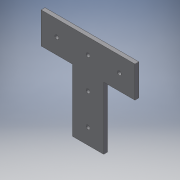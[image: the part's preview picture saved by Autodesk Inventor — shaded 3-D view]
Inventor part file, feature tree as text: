
AUTODESK INVENTOR PART (.ipt)
format: ipt  version: 2018 (Build 220112000, 112)  size: 117,248 bytes
history: native  units: in
note: dims shown in document units (in); Inventor stores cm internally (conversion verified against a paired STEP export)
features: extrude x1, sketch x1
ambient origin geometry x8: Origin, YZ Plane, XZ Plane, XY Plane, X Axis, Y Axis, Z Axis, Center Point
bodies: Solid1 (feature_tree)
feature tree (2):
  extrude  "Extrusion1"  Depth=3.0in
  sketch  "Sketch1"  dims[d0=1.0in d1=3.0in d2=3.0in d3=1.0in d4=0.2031in d5=1.0in d6=1.0in d7=1.0in d8=1.0in d9=0.125in d10=0.0in d11=0.2031in d12=0.2031in d13=0.2031in d14=0.2031in]
